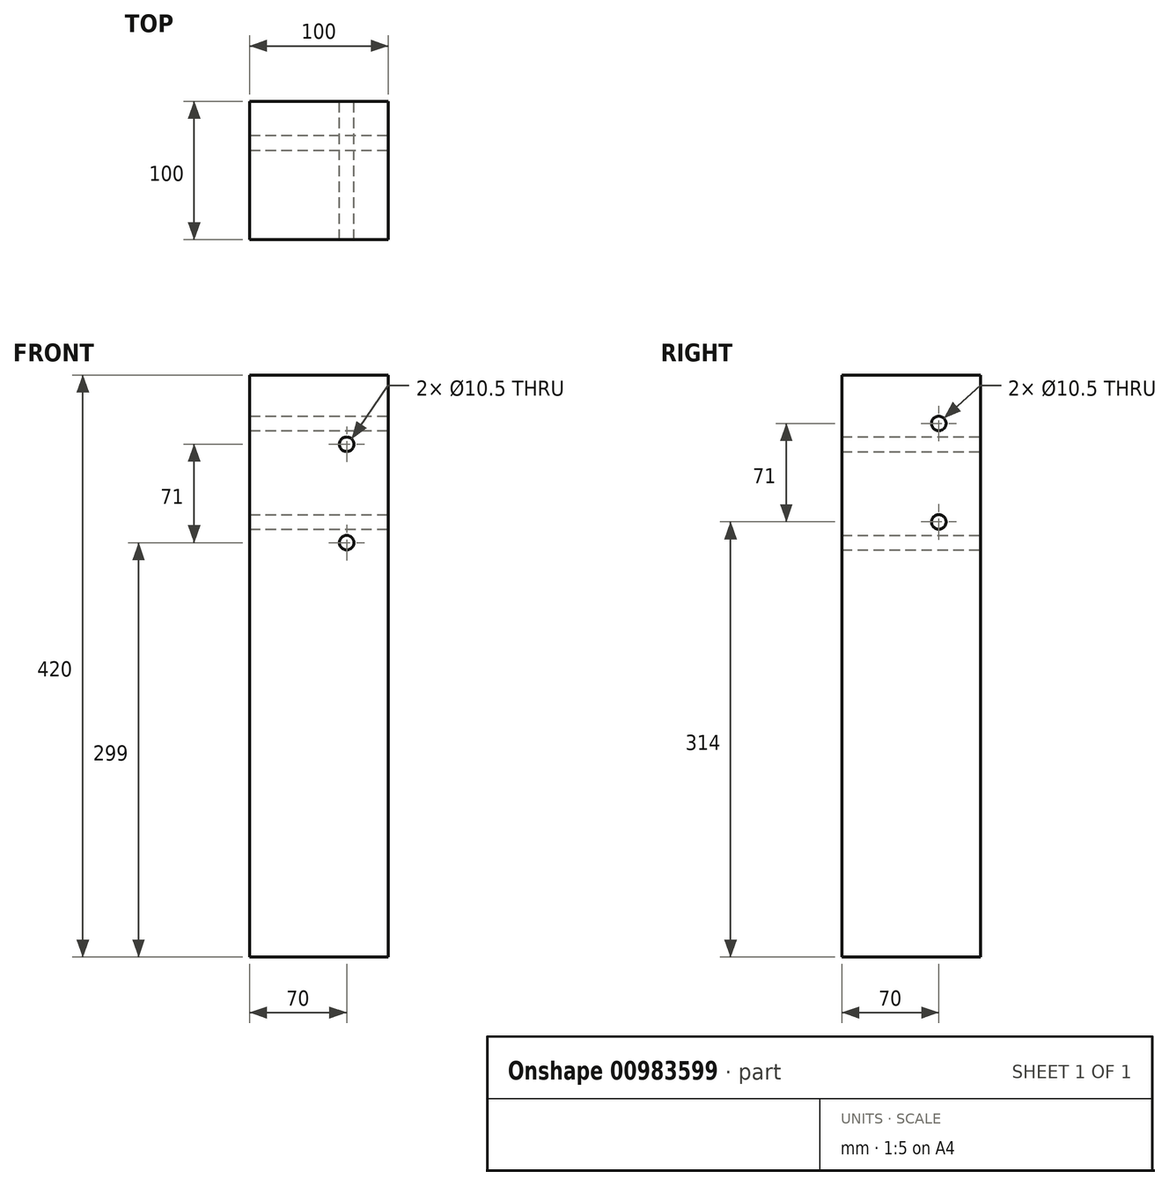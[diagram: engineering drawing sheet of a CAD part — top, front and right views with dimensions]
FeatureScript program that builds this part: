
annotation { "Feature Type Name" : "Feature", "Feature Type Description" : "" }
export const myFeature = defineFeature(function(context is Context, id is Id, definition is map)
    precondition{}
    {
        {
            var Q0;
            Q0=qCreatedBy(makeId("Top.planeOp"),FACE);
            var sketch = newSketch(context, id + "F0", { "sketchPlane" : qUnion([Q0])});
            skLineSegment(sketch, "E0.bottom", {"start": v(50, -50) * mm, "end": v(-50, -50) * mm});
            skLineSegment(sketch, "E0.top", {"start": v(50, 50) * mm, "end": v(-50, 50) * mm});
            skLineSegment(sketch, "E0.left", {"start": v(50, -50) * mm, "end": v(50, 50) * mm});
            skLineSegment(sketch, "E0.right", {"start": v(-50, -50) * mm, "end": v(-50, 50) * mm});
            skPoint(sketch, "E0.middle", {"position": v(0, 0) * mm});
            skSolve(sketch);
        }
        {
            var Q0;
            Q0=makeQuery(id+"F0.imprint","IMPRINT",FACE,{"disambiguationData":[TD([[makeQuery(id+"F0.imprint","IMPRINT",EDGE,{"derivedFrom":sQuery(id+"F0.wireOp",EDGE,"E0.bottom")}),-1.0]])]});
            extrude(context, id + "F1", {"entities" : qUnion([Q0]), "flatOperationType" : FlatOperationType.REMOVE, "oppositeDirection" : true, "depth" : 420 * mm, "offsetDistance" : 25 * mm, "domain" : OperationDomain.MODEL});
        }
        {
            var Q0;
            Q0=makeQuery(id+"F1.opExtrude","SWEPT_FACE",FACE,{"disambiguationData":[OSD([sQuery(id+"F0.wireOp",EDGE,"E0.left")])]});
            var sketch = newSketch(context, id + "F2", { "sketchPlane" : qUnion([Q0])});
            skLineSegment(sketch, "E1", {"start": v(20, 0) * mm, "end": v(20, -163.87) * mm, "construction": true});
            skCircle(sketch, "E2", {"center": v(20, -35) * mm, "radius": 5.25 * mm});
            skCircle(sketch, "E3", {"center": v(20, -106) * mm, "radius": 5.25 * mm});
            skSolve(sketch);
        }
        {
            var Q0;
            Q0=makeQuery(id+"F2.imprint","IMPRINT",FACE,{"disambiguationData":[TD([[makeQuery(id+"F2.imprint","IMPRINT",EDGE,{"derivedFrom":sQuery(id+"F2.wireOp",EDGE,"E2")}),1.0]])]});
            var Q1;
            Q1=makeQuery(id+"F2.imprint","IMPRINT",FACE,{"disambiguationData":[TD([[makeQuery(id+"F2.imprint","IMPRINT",EDGE,{"derivedFrom":sQuery(id+"F2.wireOp",EDGE,"E3")}),1.0]])]});
            extrude(context, id + "F3", {"entities" : qUnion([Q0, Q1]), "operationType" : NewBodyOperationType.REMOVE, "endBound" : BoundingType.THROUGH_ALL, "oppositeDirection" : true, "depth" : 25 * mm, "offsetDistance" : 25 * mm});
        }
        {
            var Q0;
            Q0=makeQuery(id+"F1.opExtrude","SWEPT_FACE",FACE,{"disambiguationData":[OSD([sQuery(id+"F0.wireOp",EDGE,"E0.top")])]});
            var sketch = newSketch(context, id + "F4", { "sketchPlane" : qUnion([Q0])});
            skLineSegment(sketch, "E4", {"start": v(-20, 0) * mm, "end": v(-20, -224.43) * mm, "construction": true});
            skCircle(sketch, "E5", {"center": v(-20, -50) * mm, "radius": 5.25 * mm});
            skCircle(sketch, "E6", {"center": v(-20, -121) * mm, "radius": 5.25 * mm});
            skSolve(sketch);
        }
        {
            var Q0;
            Q0=makeQuery(id+"F4.imprint","IMPRINT",FACE,{"disambiguationData":[TD([[makeQuery(id+"F4.imprint","IMPRINT",EDGE,{"derivedFrom":sQuery(id+"F4.wireOp",EDGE,"E5")}),1.0]])]});
            var Q1;
            Q1=makeQuery(id+"F4.imprint","IMPRINT",FACE,{"disambiguationData":[TD([[makeQuery(id+"F4.imprint","IMPRINT",EDGE,{"derivedFrom":sQuery(id+"F4.wireOp",EDGE,"E6")}),1.0]])]});
            extrude(context, id + "F5", {"entities" : qUnion([Q0, Q1]), "operationType" : NewBodyOperationType.REMOVE, "endBound" : BoundingType.THROUGH_ALL, "oppositeDirection" : true, "depth" : 25 * mm, "offsetDistance" : 25 * mm});
        }
    });
